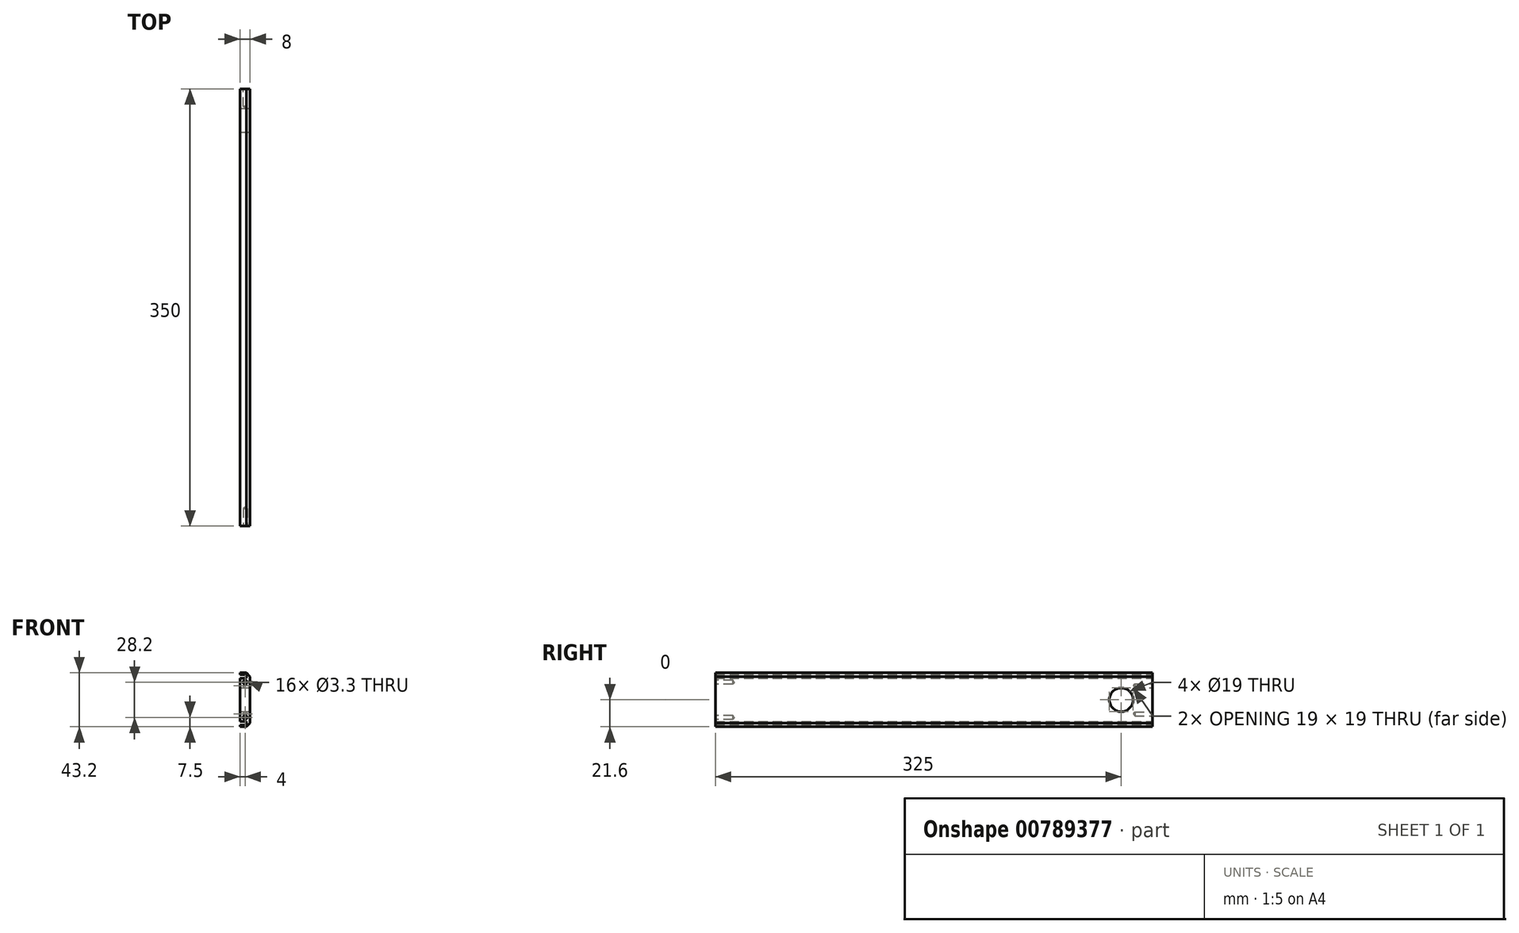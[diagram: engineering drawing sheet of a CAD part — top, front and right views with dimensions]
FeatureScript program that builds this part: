
annotation { "Feature Type Name" : "Feature", "Feature Type Description" : "" }
export const myFeature = defineFeature(function(context is Context, id is Id, definition is map)
    precondition{}
    {
        {
            var Q0;
            Q0=qCreatedBy(makeId("Front.planeOp"),FACE);
            var sketch = newSketch(context, id + "F0", { "sketchPlane" : qUnion([Q0])});
            skLineSegment(sketch, "E0", {"start": v(-3, 17.25) * mm, "end": v(2, 17.25) * mm});
            skLineSegment(sketch, "E1", {"start": v(2, 17.25) * mm, "end": v(2, 20.25) * mm});
            skLineSegment(sketch, "E2", {"start": v(2, 20.25) * mm, "end": v(-3, 20.25) * mm});
            skLineSegment(sketch, "E3", {"start": v(-3, 20.25) * mm, "end": v(-3, 21.6) * mm});
            skLineSegment(sketch, "E4", {"start": v(-3, 21.6) * mm, "end": v(5, 21.6) * mm});
            skLineSegment(sketch, "E5", {"start": v(5, 21.6) * mm, "end": v(5, -21.6) * mm});
            skLineSegment(sketch, "E6", {"start": v(5, -21.6) * mm, "end": v(-3, -21.6) * mm});
            skLineSegment(sketch, "E7", {"start": v(-3, -21.6) * mm, "end": v(-3, -20.25) * mm});
            skLineSegment(sketch, "E8", {"start": v(-3, -20.25) * mm, "end": v(2, -20.25) * mm});
            skLineSegment(sketch, "E9", {"start": v(2, -20.25) * mm, "end": v(2, -17.25) * mm});
            skLineSegment(sketch, "E10", {"start": v(2, -17.25) * mm, "end": v(-3, -17.25) * mm});
            skLineSegment(sketch, "E11", {"start": v(-3, -17.25) * mm, "end": v(-3, 17.25) * mm});
            skSolve(sketch);
        }
        {
            var Q0;
            Q0=makeQuery(id+"F0.imprint","IMPRINT",FACE,{"disambiguationData":[TD([[makeQuery(id+"F0.imprint","IMPRINT",EDGE,{"derivedFrom":sQuery(id+"F0.wireOp",EDGE,"E0")}),-1.0]])]});
            extrude(context, id + "F1", {"entities" : qUnion([Q0]), "depth" : 350 * mm, "offsetDistance" : 25 * mm});
        }
        {
            var Q0;
            Q0=makeQuery(id+"F1.opExtrude","SWEPT_EDGE",EDGE,{"disambiguationData":[OSD([sQuery(id+"F0.wireOp",EDGE,"E5"),sQuery(id+"F0.wireOp",EDGE,"E6")])]});
            var Q1;
            Q1=makeQuery(id+"F1.opExtrude","SWEPT_EDGE",EDGE,{"disambiguationData":[OSD([sQuery(id+"F0.wireOp",EDGE,"E4"),sQuery(id+"F0.wireOp",EDGE,"E5")])]});
            chamfer(context, id + "F2", {"entities" : qUnion([Q0, Q1]), "width" : 3 * mm, "tangentPropagation" : true});
        }
        {
            var Q0;
            Q0=makeQuery(id+"F1.opExtrude","SWEPT_FACE",FACE,{"disambiguationData":[OSD([sQuery(id+"F0.wireOp",EDGE,"E5")])]});
            var sketch = newSketch(context, id + "F3", { "sketchPlane" : qUnion([Q0])});
            skPoint(sketch, "E12", {"position": v(-25, 0) * mm});
            skSolve(sketch);
        }
        {
            var Q0;
            Q0=sQuery(id+"F3.wireOp",VERTEX,"E12");
            var Q1;
            Q1=makeQuery(id+"F1.opExtrude","SWEPT_BODY",BODY,{"disambiguationData":[OSD([sQuery(id+"F0.wireOp",EDGE,"E0"),sQuery(id+"F0.wireOp",EDGE,"E1"),sQuery(id+"F0.wireOp",EDGE,"E2"),sQuery(id+"F0.wireOp",EDGE,"E3"),sQuery(id+"F0.wireOp",EDGE,"E4"),sQuery(id+"F0.wireOp",EDGE,"E5"),sQuery(id+"F0.wireOp",EDGE,"E6"),sQuery(id+"F0.wireOp",EDGE,"E7"),sQuery(id+"F0.wireOp",EDGE,"E8"),sQuery(id+"F0.wireOp",EDGE,"E9"),sQuery(id+"F0.wireOp",EDGE,"E10"),sQuery(id+"F0.wireOp",EDGE,"E11")])]});
            hole(context, id + "F4", {"style" : HoleStyle.SIMPLE, "endStyle" : HoleEndStyle.THROUGH, "holeDiameter" : 19 * mm, "majorDiameter" : 5 * mm, "isTappedThrough" : true, "tappedDepth" : 12 * mm, "tapClearance" : 3, "locations" : qUnion([Q0]), "scope" : qUnion([Q1])});
        }
        {
            var Q0;
            Q0=qCreatedBy(makeId("Front.planeOp"),FACE);
            var sketch = newSketch(context, id + "F5", { "sketchPlane" : qUnion([Q0])});
            skPoint(sketch, "E13", {"position": v(1, 11.28) * mm});
            skPoint(sketch, "E14", {"position": v(1, -11.28) * mm});
            skSolve(sketch);
        }
        {
            var Q0;
            Q0=sQuery(id+"F5.wireOp",VERTEX,"E13");
            var Q1;
            Q1=sQuery(id+"F5.wireOp",VERTEX,"E14");
            var Q2;
            Q2=makeQuery(id+"F1.opExtrude","SWEPT_BODY",BODY,{"disambiguationData":[OSD([sQuery(id+"F0.wireOp",EDGE,"E0"),sQuery(id+"F0.wireOp",EDGE,"E1"),sQuery(id+"F0.wireOp",EDGE,"E2"),sQuery(id+"F0.wireOp",EDGE,"E3"),sQuery(id+"F0.wireOp",EDGE,"E4"),sQuery(id+"F0.wireOp",EDGE,"E5"),sQuery(id+"F0.wireOp",EDGE,"E6"),sQuery(id+"F0.wireOp",EDGE,"E7"),sQuery(id+"F0.wireOp",EDGE,"E8"),sQuery(id+"F0.wireOp",EDGE,"E9"),sQuery(id+"F0.wireOp",EDGE,"E10"),sQuery(id+"F0.wireOp",EDGE,"E11")])]});
            hole(context, id + "F6", {"style" : HoleStyle.SIMPLE, "endStyle" : HoleEndStyle.BLIND, "oppositeDirection" : true, "standardTappedOrClearance" : lookupTablePath({ "standard" : "ISO", "engagement" : "75%", "pitch" : "0.7 mm", "size" : "M4", "type" : "Tapped" }), "standardBlindInLast" : lookupTablePath({ "standard" : "ISO", "engagement" : "75%", "pitch" : "0.7 mm", "size" : "M4", "type" : "Tapped" }), "holeDiameter" : 3.3 * mm, "majorDiameter" : 4 * mm, "showTappedDepth" : true, "holeDepth" : 14.1 * mm, "isTappedThrough" : true, "tappedDepth" : 12 * mm, "tapClearance" : 3, "startFromSketch" : true, "locations" : qUnion([Q0, Q1]), "scope" : qUnion([Q2])});
        }
        {
            var Q0;
            Q0=makeQuery(id+"F1.opExtrude","CAP_FACE",FACE,{"disambiguationData":[OSD([sQuery(id+"F0.wireOp",EDGE,"E0"),sQuery(id+"F0.wireOp",EDGE,"E1"),sQuery(id+"F0.wireOp",EDGE,"E2"),sQuery(id+"F0.wireOp",EDGE,"E3"),sQuery(id+"F0.wireOp",EDGE,"E4"),sQuery(id+"F0.wireOp",EDGE,"E5"),sQuery(id+"F0.wireOp",EDGE,"E6"),sQuery(id+"F0.wireOp",EDGE,"E7"),sQuery(id+"F0.wireOp",EDGE,"E8"),sQuery(id+"F0.wireOp",EDGE,"E9"),sQuery(id+"F0.wireOp",EDGE,"E10"),sQuery(id+"F0.wireOp",EDGE,"E11")])],"isStart":false});
            var sketch = newSketch(context, id + "F7", { "sketchPlane" : qUnion([Q0])});
            skPoint(sketch, "E15", {"position": v(1, -14.1) * mm});
            skPoint(sketch, "E16", {"position": v(1, 14.1) * mm});
            skSolve(sketch);
        }
        {
            var Q0;
            Q0=sQuery(id+"F7.wireOp",VERTEX,"E16");
            var Q1;
            Q1=sQuery(id+"F7.wireOp",VERTEX,"E15");
            var Q2;
            Q2=makeQuery(id+"F1.opExtrude","SWEPT_BODY",BODY,{"disambiguationData":[OSD([sQuery(id+"F0.wireOp",EDGE,"E0"),sQuery(id+"F0.wireOp",EDGE,"E1"),sQuery(id+"F0.wireOp",EDGE,"E2"),sQuery(id+"F0.wireOp",EDGE,"E3"),sQuery(id+"F0.wireOp",EDGE,"E4"),sQuery(id+"F0.wireOp",EDGE,"E5"),sQuery(id+"F0.wireOp",EDGE,"E6"),sQuery(id+"F0.wireOp",EDGE,"E7"),sQuery(id+"F0.wireOp",EDGE,"E8"),sQuery(id+"F0.wireOp",EDGE,"E9"),sQuery(id+"F0.wireOp",EDGE,"E10"),sQuery(id+"F0.wireOp",EDGE,"E11")])]});
            hole(context, id + "F8", {"style" : HoleStyle.SIMPLE, "endStyle" : HoleEndStyle.BLIND, "standardTappedOrClearance" : lookupTablePath({ "standard" : "ISO", "engagement" : "75%", "pitch" : "0.7 mm", "size" : "M4", "type" : "Tapped" }), "standardBlindInLast" : lookupTablePath({ "standard" : "ISO", "engagement" : "75%", "pitch" : "0.7 mm", "size" : "M4", "type" : "Tapped" }), "holeDiameter" : 3.3 * mm, "majorDiameter" : 4 * mm, "showTappedDepth" : true, "holeDepth" : 14.1 * mm, "isTappedThrough" : true, "tappedDepth" : 12 * mm, "tapClearance" : 3, "startFromSketch" : true, "locations" : qUnion([Q0, Q1]), "scope" : qUnion([Q2])});
        }
    });
